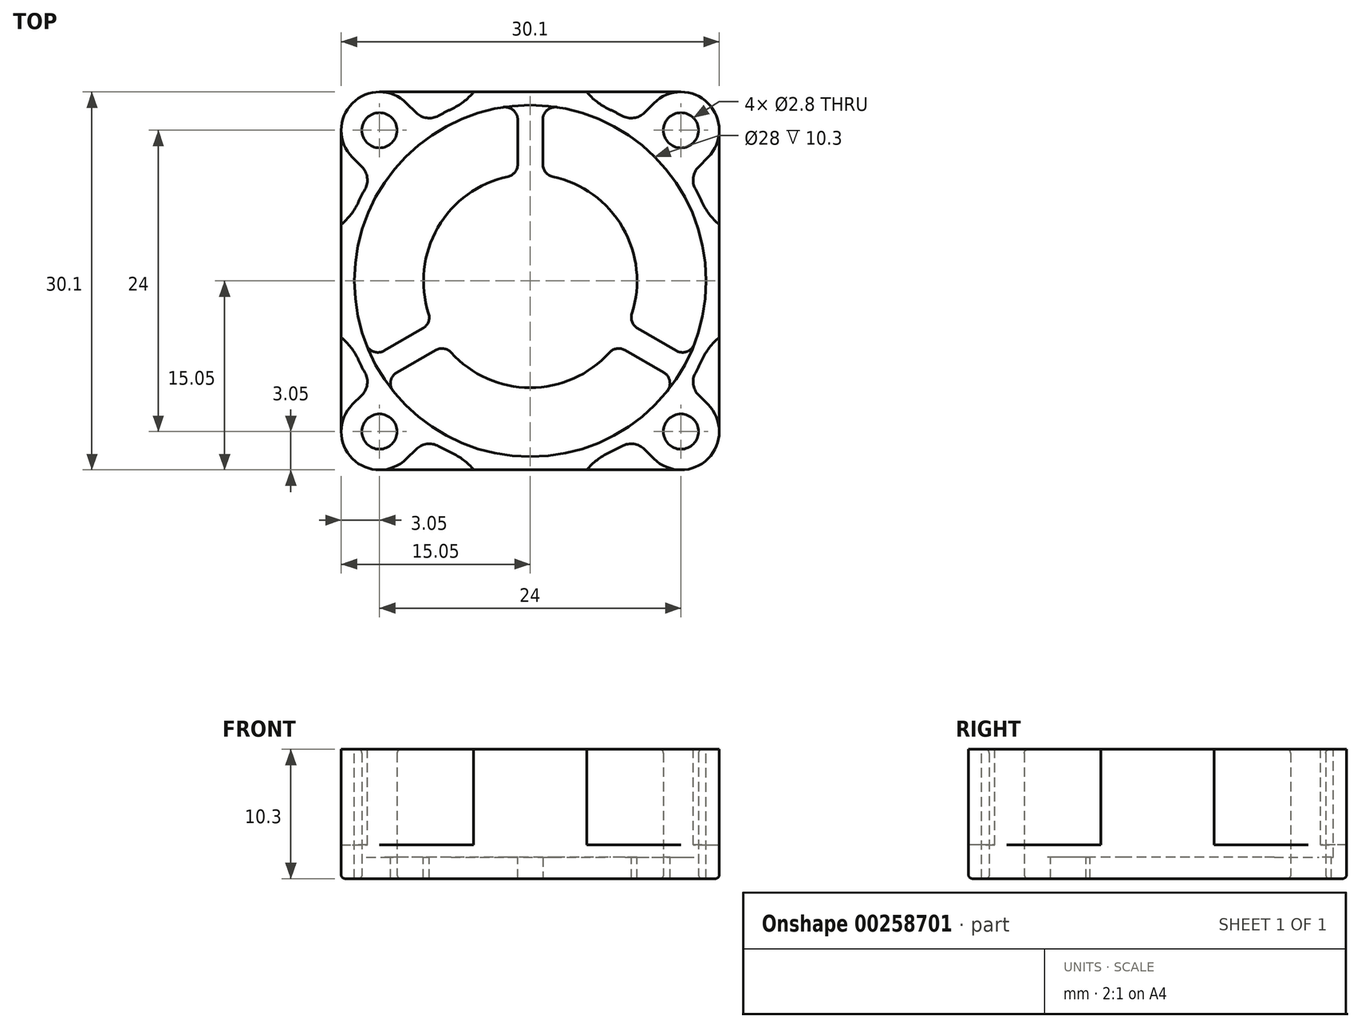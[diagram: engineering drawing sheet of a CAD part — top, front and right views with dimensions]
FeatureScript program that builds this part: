
annotation { "Feature Type Name" : "Feature", "Feature Type Description" : "" }
export const myFeature = defineFeature(function(context is Context, id is Id, definition is map)
    precondition{}
    {
        {
            var Q0;
            Q0=qCreatedBy(makeId("Top.planeOp"),FACE);
            var sketch = newSketch(context, id + "F0", { "sketchPlane" : qUnion([Q0])});
            skLineSegment(sketch, "E0.bottom", {"start": v(-15.05, 15.05) * mm, "end": v(15.05, 15.05) * mm});
            skLineSegment(sketch, "E0.top", {"start": v(-15.05, -15.05) * mm, "end": v(15.05, -15.05) * mm});
            skLineSegment(sketch, "E0.left", {"start": v(-15.05, 15.05) * mm, "end": v(-15.05, -15.05) * mm});
            skLineSegment(sketch, "E0.right", {"start": v(15.05, 15.05) * mm, "end": v(15.05, -15.05) * mm});
            skPoint(sketch, "E0.middle", {"position": v(0, 0) * mm});
            skCircle(sketch, "E1", {"center": v(-12, -12) * mm, "radius": 1.4 * mm});
            skCircle(sketch, "E2", {"center": v(12, -12) * mm, "radius": 1.4 * mm});
            skCircle(sketch, "E3", {"center": v(-12, 12) * mm, "radius": 1.4 * mm});
            skCircle(sketch, "E4", {"center": v(12, 12) * mm, "radius": 1.4 * mm});
            skSolve(sketch);
        }
        {
            var Q0;
            Q0=makeQuery(id+"F0.imprint","IMPRINT",FACE,{"disambiguationData":[TD([[makeQuery(id+"F0.imprint","IMPRINT",EDGE,{"derivedFrom":sQuery(id+"F0.wireOp",EDGE,"E0.bottom")}),-1.0]])]});
            extrude(context, id + "F1", {"entities" : qUnion([Q0]), "depth" : 10.3 * mm});
        }
        {
            var Q0;
            Q0=makeQuery(id+"F1.opExtrude","SWEPT_EDGE",EDGE,{"disambiguationData":[OSD([sQuery(id+"F0.wireOp",EDGE,"E0.top"),sQuery(id+"F0.wireOp",EDGE,"E0.left")])]});
            var Q1;
            Q1=makeQuery(id+"F1.opExtrude","SWEPT_EDGE",EDGE,{"disambiguationData":[OSD([sQuery(id+"F0.wireOp",EDGE,"E0.bottom"),sQuery(id+"F0.wireOp",EDGE,"E0.left")])]});
            var Q2;
            Q2=makeQuery(id+"F1.opExtrude","SWEPT_EDGE",EDGE,{"disambiguationData":[OSD([sQuery(id+"F0.wireOp",EDGE,"E0.top"),sQuery(id+"F0.wireOp",EDGE,"E0.right")])]});
            var Q3;
            Q3=makeQuery(id+"F1.opExtrude","SWEPT_EDGE",EDGE,{"disambiguationData":[OSD([sQuery(id+"F0.wireOp",EDGE,"E0.bottom"),sQuery(id+"F0.wireOp",EDGE,"E0.right")])]});
            fillet(context, id + "F2", {"entities" : qUnion([Q0, Q1, Q2, Q3]), "radius" : 3.05 * mm, "tangentPropagation" : true, "allowEdgeOverflow" : false});
        }
        {
            var Q0;
            Q0=makeQuery(id+"F1.opExtrude","CAP_FACE",FACE,{"disambiguationData":[OSD([sQuery(id+"F0.wireOp",EDGE,"E0.bottom"),sQuery(id+"F0.wireOp",EDGE,"E0.top"),sQuery(id+"F0.wireOp",EDGE,"E0.left"),sQuery(id+"F0.wireOp",EDGE,"E0.right"),sQuery(id+"F0.wireOp",EDGE,"E1"),sQuery(id+"F0.wireOp",EDGE,"E2"),sQuery(id+"F0.wireOp",EDGE,"E3"),sQuery(id+"F0.wireOp",EDGE,"E4")])],"isStart":false});
            var sketch = newSketch(context, id + "F3", { "sketchPlane" : qUnion([Q0])});
            skCircle(sketch, "E5", {"center": v(0, 0) * mm, "radius": 14 * mm});
            skCircle(sketch, "E6", {"center": v(0, 0) * mm, "radius": 15.05 * mm});
            skCircle(sketch, "E7", {"center": v(-12, 12) * mm, "radius": 3.05 * mm});
            skCircle(sketch, "E8", {"center": v(12, 12) * mm, "radius": 3.05 * mm});
            skCircle(sketch, "E9", {"center": v(-12, -12) * mm, "radius": 3.05 * mm});
            skCircle(sketch, "E10", {"center": v(12, -12) * mm, "radius": 3.05 * mm});
            skLineSegment(sketch, "E11", {"start": v(-14.16, 9.84) * mm, "end": v(9.84, -14.16) * mm});
            skLineSegment(sketch, "E12", {"start": v(14.16, -9.84) * mm, "end": v(-9.84, 14.16) * mm});
            skLineSegment(sketch, "E13", {"start": v(9.84, 14.16) * mm, "end": v(-14.16, -9.84) * mm});
            skLineSegment(sketch, "E14", {"start": v(-9.84, -14.16) * mm, "end": v(14.16, 9.84) * mm});
            skLineSegment(sketch, "E15.bottom", {"start": v(-15.05, 4.5) * mm, "end": v(15.05, 4.5) * mm});
            skLineSegment(sketch, "E15.top", {"start": v(-15.05, -4.5) * mm, "end": v(15.05, -4.5) * mm});
            skLineSegment(sketch, "E15.left", {"start": v(-15.05, 4.5) * mm, "end": v(-15.05, -4.5) * mm});
            skLineSegment(sketch, "E15.right", {"start": v(15.05, 4.5) * mm, "end": v(15.05, -4.5) * mm});
            skLineSegment(sketch, "E16.bottom", {"start": v(4.5, 15.05) * mm, "end": v(-4.5, 15.05) * mm});
            skLineSegment(sketch, "E16.top", {"start": v(4.5, -15.05) * mm, "end": v(-4.5, -15.05) * mm});
            skLineSegment(sketch, "E16.left", {"start": v(4.5, 15.05) * mm, "end": v(4.5, -15.05) * mm});
            skLineSegment(sketch, "E16.right", {"start": v(-4.5, 15.05) * mm, "end": v(-4.5, -15.05) * mm});
            skSolve(sketch);
        }
        {
            var Q0;
            {var subQ0=sQuery(id+"F3.wireOp",EDGE,"E11");var subQ3=sQuery(id+"F3.wireOp",EDGE,"E6");var subQ4=makeQuery(id+"F3.imprint","INTERSECT",VERTEX,{"disambiguationData":[OD(0.0)],"derivedFrom":[subQ3,subQ0]});Q0=makeQuery(id+"F3.imprint","IMPRINT",FACE,{"disambiguationData":[TD([[makeQuery(id+"F3.imprint","IMPRINT",EDGE,{"disambiguationData":[TD([[subQ4,-1.0]])],"derivedFrom":subQ3}),-1.0]])]});}
            var Q1;
            {var subQ3=sQuery(id+"F3.wireOp",EDGE,"E6");var subQ7=sQuery(id+"F3.wireOp",EDGE,"E15.top");var subQ9=makeQuery(id+"F3.imprint","INTERSECT",VERTEX,{"disambiguationData":[OD(0.0)],"derivedFrom":[subQ3,subQ7]});Q1=makeQuery(id+"F3.imprint","IMPRINT",FACE,{"disambiguationData":[TD([[makeQuery(id+"F3.imprint","IMPRINT",EDGE,{"disambiguationData":[TD([[subQ9,-1.0]])],"derivedFrom":subQ3}),-1.0]])]});}
            var Q2;
            {var subQ3=sQuery(id+"F3.wireOp",EDGE,"E6");var subQ5=sQuery(id+"F3.wireOp",EDGE,"E14");var subQ8=makeQuery(id+"F3.imprint","INTERSECT",VERTEX,{"disambiguationData":[OD(1.0)],"derivedFrom":[subQ3,subQ5]});Q2=makeQuery(id+"F3.imprint","IMPRINT",FACE,{"disambiguationData":[TD([[makeQuery(id+"F3.imprint","IMPRINT",EDGE,{"disambiguationData":[TD([[subQ8,-1.0]])],"derivedFrom":subQ3}),-1.0]])]});}
            var Q3;
            {var subQ0=sQuery(id+"F3.wireOp",EDGE,"E16.left");var subQ3=sQuery(id+"F3.wireOp",EDGE,"E6");var subQ4=makeQuery(id+"F3.imprint","INTERSECT",VERTEX,{"disambiguationData":[OD(1.0)],"derivedFrom":[subQ3,subQ0]});Q3=makeQuery(id+"F3.imprint","IMPRINT",FACE,{"disambiguationData":[TD([[makeQuery(id+"F3.imprint","IMPRINT",EDGE,{"disambiguationData":[TD([[subQ4,-1.0]])],"derivedFrom":subQ3}),-1.0]])]});}
            var Q4;
            {var subQ0=sQuery(id+"F3.wireOp",EDGE,"E12");var subQ3=sQuery(id+"F3.wireOp",EDGE,"E6");var subQ4=makeQuery(id+"F3.imprint","INTERSECT",VERTEX,{"disambiguationData":[OD(1.0)],"derivedFrom":[subQ3,subQ0]});Q4=makeQuery(id+"F3.imprint","IMPRINT",FACE,{"disambiguationData":[TD([[makeQuery(id+"F3.imprint","IMPRINT",EDGE,{"disambiguationData":[TD([[subQ4,-1.0]])],"derivedFrom":subQ3}),-1.0]])]});}
            var Q5;
            {var subQ0=sQuery(id+"F3.wireOp",EDGE,"E15.bottom");var subQ3=sQuery(id+"F3.wireOp",EDGE,"E6");var subQ4=makeQuery(id+"F3.imprint","INTERSECT",VERTEX,{"disambiguationData":[OD(0.0)],"derivedFrom":[subQ3,subQ0]});Q5=makeQuery(id+"F3.imprint","IMPRINT",FACE,{"disambiguationData":[TD([[makeQuery(id+"F3.imprint","IMPRINT",EDGE,{"disambiguationData":[TD([[subQ4,-1.0]])],"derivedFrom":subQ3}),-1.0]])]});}
            var Q6;
            {var subQ3=sQuery(id+"F3.wireOp",EDGE,"E13");var subQ7=sQuery(id+"F3.wireOp",EDGE,"E6");var subQ9=makeQuery(id+"F3.imprint","INTERSECT",VERTEX,{"disambiguationData":[OD(0.0)],"derivedFrom":[subQ7,subQ3]});Q6=makeQuery(id+"F3.imprint","IMPRINT",FACE,{"disambiguationData":[TD([[makeQuery(id+"F3.imprint","IMPRINT",EDGE,{"disambiguationData":[TD([[subQ9,-1.0]])],"derivedFrom":subQ7}),-1.0]])]});}
            var Q7;
            {var subQ0=sQuery(id+"F3.wireOp",EDGE,"E16.right");var subQ3=sQuery(id+"F3.wireOp",EDGE,"E6");var subQ4=makeQuery(id+"F3.imprint","INTERSECT",VERTEX,{"disambiguationData":[OD(0.0)],"derivedFrom":[subQ3,subQ0]});Q7=makeQuery(id+"F3.imprint","IMPRINT",FACE,{"disambiguationData":[TD([[makeQuery(id+"F3.imprint","IMPRINT",EDGE,{"disambiguationData":[TD([[subQ4,-1.0]])],"derivedFrom":subQ3}),-1.0]])]});}
            var Q8;
            {var subQ1=sQuery(id+"F3.wireOp",EDGE,"E5");var subQ8=sQuery(id+"F3.wireOp",EDGE,"E12");var subQ9=makeQuery(id+"F3.imprint","INTERSECT",VERTEX,{"disambiguationData":[OD(0.0)],"derivedFrom":[subQ1,subQ8]});Q8=makeQuery(id+"F3.imprint","IMPRINT",FACE,{"disambiguationData":[TD([[makeQuery(id+"F3.imprint","IMPRINT",EDGE,{"disambiguationData":[TD([[subQ9,-1.0]])],"derivedFrom":subQ1}),1.0]])]});}
            var Q9;
            {var subQ0=sQuery(id+"F3.wireOp",EDGE,"E11");var subQ1=sQuery(id+"F3.wireOp",EDGE,"E5");var subQ2=makeQuery(id+"F3.imprint","INTERSECT",VERTEX,{"disambiguationData":[OD(0.0)],"derivedFrom":[subQ1,subQ0]});Q9=makeQuery(id+"F3.imprint","IMPRINT",FACE,{"disambiguationData":[TD([[makeQuery(id+"F3.imprint","IMPRINT",EDGE,{"disambiguationData":[TD([[subQ2,-1.0]])],"derivedFrom":subQ1}),1.0]])]});}
            var Q10;
            {var subQ0=sQuery(id+"F3.wireOp",EDGE,"E15.bottom");var subQ1=sQuery(id+"F3.wireOp",EDGE,"E5");var subQ2=makeQuery(id+"F3.imprint","INTERSECT",VERTEX,{"disambiguationData":[OD(1.0)],"derivedFrom":[subQ1,subQ0]});Q10=makeQuery(id+"F3.imprint","IMPRINT",FACE,{"disambiguationData":[TD([[makeQuery(id+"F3.imprint","IMPRINT",EDGE,{"disambiguationData":[TD([[subQ2,-1.0]])],"derivedFrom":subQ1}),1.0]])]});}
            var Q11;
            {var subQ0=sQuery(id+"F3.wireOp",EDGE,"E15.top");var subQ1=sQuery(id+"F3.wireOp",EDGE,"E5");var subQ2=makeQuery(id+"F3.imprint","INTERSECT",VERTEX,{"disambiguationData":[OD(0.0)],"derivedFrom":[subQ1,subQ0]});Q11=makeQuery(id+"F3.imprint","IMPRINT",FACE,{"disambiguationData":[TD([[makeQuery(id+"F3.imprint","IMPRINT",EDGE,{"disambiguationData":[TD([[subQ2,-1.0]])],"derivedFrom":subQ1}),1.0]])]});}
            var Q12;
            {var subQ0=sQuery(id+"F3.wireOp",EDGE,"E13");var subQ1=sQuery(id+"F3.wireOp",EDGE,"E5");var subQ2=makeQuery(id+"F3.imprint","INTERSECT",VERTEX,{"disambiguationData":[OD(1.0)],"derivedFrom":[subQ1,subQ0]});Q12=makeQuery(id+"F3.imprint","IMPRINT",FACE,{"disambiguationData":[TD([[makeQuery(id+"F3.imprint","IMPRINT",EDGE,{"disambiguationData":[TD([[subQ2,-1.0]])],"derivedFrom":subQ1}),1.0]])]});}
            var Q13;
            {var subQ0=sQuery(id+"F3.wireOp",EDGE,"E16.right");var subQ9=sQuery(id+"F3.wireOp",EDGE,"E5");var subQ10=makeQuery(id+"F3.imprint","INTERSECT",VERTEX,{"disambiguationData":[OD(1.0)],"derivedFrom":[subQ9,subQ0]});Q13=makeQuery(id+"F3.imprint","IMPRINT",FACE,{"disambiguationData":[TD([[makeQuery(id+"F3.imprint","IMPRINT",EDGE,{"disambiguationData":[TD([[subQ10,-1.0]])],"derivedFrom":subQ9}),1.0]])]});}
            var Q14;
            {var subQ0=sQuery(id+"F3.wireOp",EDGE,"E14");var subQ1=sQuery(id+"F3.wireOp",EDGE,"E5");var subQ2=makeQuery(id+"F3.imprint","INTERSECT",VERTEX,{"disambiguationData":[OD(1.0)],"derivedFrom":[subQ1,subQ0]});Q14=makeQuery(id+"F3.imprint","IMPRINT",FACE,{"disambiguationData":[TD([[makeQuery(id+"F3.imprint","IMPRINT",EDGE,{"disambiguationData":[TD([[subQ2,-1.0]])],"derivedFrom":subQ1}),1.0]])]});}
            var Q15;
            {var subQ0=sQuery(id+"F3.wireOp",EDGE,"E16.left");var subQ1=sQuery(id+"F3.wireOp",EDGE,"E5");var subQ2=makeQuery(id+"F3.imprint","INTERSECT",VERTEX,{"disambiguationData":[OD(1.0)],"derivedFrom":[subQ1,subQ0]});Q15=makeQuery(id+"F3.imprint","IMPRINT",FACE,{"disambiguationData":[TD([[makeQuery(id+"F3.imprint","IMPRINT",EDGE,{"disambiguationData":[TD([[subQ2,-1.0]])],"derivedFrom":subQ1}),1.0]])]});}
            var Q16;
            {var subQ0=sQuery(id+"F3.wireOp",EDGE,"E11");var subQ1=sQuery(id+"F3.wireOp",EDGE,"E5");var subQ2=makeQuery(id+"F3.imprint","INTERSECT",VERTEX,{"disambiguationData":[OD(1.0)],"derivedFrom":[subQ1,subQ0]});Q16=makeQuery(id+"F3.imprint","IMPRINT",FACE,{"disambiguationData":[TD([[makeQuery(id+"F3.imprint","IMPRINT",EDGE,{"disambiguationData":[TD([[subQ2,-1.0]])],"derivedFrom":subQ1}),1.0]])]});}
            var Q17;
            {var subQ0=sQuery(id+"F3.wireOp",EDGE,"E12");var subQ1=sQuery(id+"F3.wireOp",EDGE,"E5");var subQ2=makeQuery(id+"F3.imprint","INTERSECT",VERTEX,{"disambiguationData":[OD(1.0)],"derivedFrom":[subQ1,subQ0]});Q17=makeQuery(id+"F3.imprint","IMPRINT",FACE,{"disambiguationData":[TD([[makeQuery(id+"F3.imprint","IMPRINT",EDGE,{"disambiguationData":[TD([[subQ2,-1.0]])],"derivedFrom":subQ1}),1.0]])]});}
            var Q18;
            {var subQ0=sQuery(id+"F3.wireOp",EDGE,"E15.bottom");var subQ1=sQuery(id+"F3.wireOp",EDGE,"E5");var subQ2=makeQuery(id+"F3.imprint","INTERSECT",VERTEX,{"disambiguationData":[OD(0.0)],"derivedFrom":[subQ1,subQ0]});Q18=makeQuery(id+"F3.imprint","IMPRINT",FACE,{"disambiguationData":[TD([[makeQuery(id+"F3.imprint","IMPRINT",EDGE,{"disambiguationData":[TD([[subQ2,1.0]])],"derivedFrom":subQ1}),1.0]])]});}
            var Q19;
            {var subQ0=sQuery(id+"F3.wireOp",EDGE,"E14");var subQ1=sQuery(id+"F3.wireOp",EDGE,"E5");var subQ2=makeQuery(id+"F3.imprint","INTERSECT",VERTEX,{"disambiguationData":[OD(0.0)],"derivedFrom":[subQ1,subQ0]});Q19=makeQuery(id+"F3.imprint","IMPRINT",FACE,{"disambiguationData":[TD([[makeQuery(id+"F3.imprint","IMPRINT",EDGE,{"disambiguationData":[TD([[subQ2,1.0]])],"derivedFrom":subQ1}),1.0]])]});}
            var Q20;
            {var subQ1=sQuery(id+"F3.wireOp",EDGE,"E5");var subQ9=sQuery(id+"F3.wireOp",EDGE,"E14");var subQ12=makeQuery(id+"F3.imprint","INTERSECT",VERTEX,{"disambiguationData":[OD(0.0)],"derivedFrom":[subQ1,subQ9]});Q20=makeQuery(id+"F3.imprint","IMPRINT",FACE,{"disambiguationData":[TD([[makeQuery(id+"F3.imprint","IMPRINT",EDGE,{"disambiguationData":[TD([[subQ12,-1.0]])],"derivedFrom":subQ1}),1.0]])]});}
            var Q21;
            {var subQ0=sQuery(id+"F3.wireOp",EDGE,"E13");var subQ1=sQuery(id+"F3.wireOp",EDGE,"E5");var subQ2=makeQuery(id+"F3.imprint","INTERSECT",VERTEX,{"disambiguationData":[OD(0.0)],"derivedFrom":[subQ1,subQ0]});Q21=makeQuery(id+"F3.imprint","IMPRINT",FACE,{"disambiguationData":[TD([[makeQuery(id+"F3.imprint","IMPRINT",EDGE,{"disambiguationData":[TD([[subQ2,-1.0]])],"derivedFrom":subQ1}),1.0]])]});}
            var Q22;
            {var subQ5=sQuery(id+"F3.wireOp",EDGE,"E16.left");var subQ9=sQuery(id+"F3.wireOp",EDGE,"E5");var subQ10=makeQuery(id+"F3.imprint","INTERSECT",VERTEX,{"disambiguationData":[OD(0.0)],"derivedFrom":[subQ9,subQ5]});Q22=makeQuery(id+"F3.imprint","IMPRINT",FACE,{"disambiguationData":[TD([[makeQuery(id+"F3.imprint","IMPRINT",EDGE,{"disambiguationData":[TD([[subQ10,-1.0]])],"derivedFrom":subQ9}),1.0]])]});}
            var Q23;
            {var subQ0=sQuery(id+"F3.wireOp",EDGE,"E16.right");var subQ1=sQuery(id+"F3.wireOp",EDGE,"E5");var subQ2=makeQuery(id+"F3.imprint","INTERSECT",VERTEX,{"disambiguationData":[OD(0.0)],"derivedFrom":[subQ1,subQ0]});Q23=makeQuery(id+"F3.imprint","IMPRINT",FACE,{"disambiguationData":[TD([[makeQuery(id+"F3.imprint","IMPRINT",EDGE,{"disambiguationData":[TD([[subQ2,-1.0]])],"derivedFrom":subQ1}),1.0]])]});}
            var Q24;
            {var subQ0=sQuery(id+"F3.wireOp",EDGE,"E15.bottom");var subQ1=sQuery(id+"F3.wireOp",EDGE,"E12");var subQ2=makeQuery(id+"F3.imprint","INTERSECT",VERTEX,{"derivedFrom":[subQ1,subQ0]});Q24=makeQuery(id+"F3.imprint","IMPRINT",FACE,{"disambiguationData":[TD([[makeQuery(id+"F3.imprint","IMPRINT",EDGE,{"disambiguationData":[TD([[subQ2,-1.0]])],"derivedFrom":subQ1}),1.0]])]});}
            var Q25;
            {var subQ0=sQuery(id+"F3.wireOp",EDGE,"E15.bottom");var subQ1=sQuery(id+"F3.wireOp",EDGE,"E11");var subQ2=makeQuery(id+"F3.imprint","INTERSECT",VERTEX,{"derivedFrom":[subQ1,subQ0]});Q25=makeQuery(id+"F3.imprint","IMPRINT",FACE,{"disambiguationData":[TD([[makeQuery(id+"F3.imprint","IMPRINT",EDGE,{"disambiguationData":[TD([[subQ2,-1.0]])],"derivedFrom":subQ1}),1.0]])]});}
            var Q26;
            {var subQ3=sQuery(id+"F3.wireOp",EDGE,"E16.right");var subQ6=sQuery(id+"F3.wireOp",EDGE,"E11");var subQ9=makeQuery(id+"F3.imprint","INTERSECT",VERTEX,{"derivedFrom":[subQ6,subQ3]});Q26=makeQuery(id+"F3.imprint","IMPRINT",FACE,{"disambiguationData":[TD([[makeQuery(id+"F3.imprint","IMPRINT",EDGE,{"disambiguationData":[TD([[subQ9,-1.0]])],"derivedFrom":subQ6}),1.0]])]});}
            var Q27;
            {var subQ0=sQuery(id+"F3.wireOp",EDGE,"E13");var subQ1=sQuery(id+"F3.wireOp",EDGE,"E11");var subQ2=makeQuery(id+"F3.imprint","INTERSECT",VERTEX,{"derivedFrom":[subQ1,subQ0]});Q27=makeQuery(id+"F3.imprint","IMPRINT",FACE,{"disambiguationData":[TD([[makeQuery(id+"F3.imprint","IMPRINT",EDGE,{"disambiguationData":[TD([[subQ2,-1.0]])],"derivedFrom":subQ1}),1.0]])]});}
            var Q28;
            {var subQ1=sQuery(id+"F3.wireOp",EDGE,"E11");var subQ5=sQuery(id+"F3.wireOp",EDGE,"E13");var subQ6=makeQuery(id+"F3.imprint","INTERSECT",VERTEX,{"derivedFrom":[subQ1,subQ5]});Q28=makeQuery(id+"F3.imprint","IMPRINT",FACE,{"disambiguationData":[TD([[makeQuery(id+"F3.imprint","IMPRINT",EDGE,{"disambiguationData":[TD([[subQ6,-1.0]])],"derivedFrom":subQ1}),-1.0]])]});}
            var Q29;
            {var subQ0=sQuery(id+"F3.wireOp",EDGE,"E16.right");var subQ1=sQuery(id+"F3.wireOp",EDGE,"E13");var subQ2=makeQuery(id+"F3.imprint","INTERSECT",VERTEX,{"derivedFrom":[subQ1,subQ0]});Q29=makeQuery(id+"F3.imprint","IMPRINT",FACE,{"disambiguationData":[TD([[makeQuery(id+"F3.imprint","IMPRINT",EDGE,{"disambiguationData":[TD([[subQ2,-1.0]])],"derivedFrom":subQ1}),1.0]])]});}
            var Q30;
            {var subQ0=sQuery(id+"F3.wireOp",EDGE,"E16.right");var subQ1=sQuery(id+"F3.wireOp",EDGE,"E14");var subQ2=makeQuery(id+"F3.imprint","INTERSECT",VERTEX,{"derivedFrom":[subQ1,subQ0]});Q30=makeQuery(id+"F3.imprint","IMPRINT",FACE,{"disambiguationData":[TD([[makeQuery(id+"F3.imprint","IMPRINT",EDGE,{"disambiguationData":[TD([[subQ2,-1.0]])],"derivedFrom":subQ1}),1.0]])]});}
            var Q31;
            {var subQ0=sQuery(id+"F3.wireOp",EDGE,"E15.top");var subQ1=sQuery(id+"F3.wireOp",EDGE,"E11");var subQ2=makeQuery(id+"F3.imprint","INTERSECT",VERTEX,{"derivedFrom":[subQ1,subQ0]});Q31=makeQuery(id+"F3.imprint","IMPRINT",FACE,{"disambiguationData":[TD([[makeQuery(id+"F3.imprint","IMPRINT",EDGE,{"disambiguationData":[TD([[subQ2,-1.0]])],"derivedFrom":subQ1}),1.0]])]});}
            var Q32;
            {var subQ0=sQuery(id+"F3.wireOp",EDGE,"E15.top");var subQ1=sQuery(id+"F3.wireOp",EDGE,"E12");var subQ2=makeQuery(id+"F3.imprint","INTERSECT",VERTEX,{"derivedFrom":[subQ1,subQ0]});Q32=makeQuery(id+"F3.imprint","IMPRINT",FACE,{"disambiguationData":[TD([[makeQuery(id+"F3.imprint","IMPRINT",EDGE,{"disambiguationData":[TD([[subQ2,-1.0]])],"derivedFrom":subQ1}),1.0]])]});}
            var Q33;
            {var subQ0=sQuery(id+"F3.wireOp",EDGE,"E16.left");var subQ1=sQuery(id+"F3.wireOp",EDGE,"E14");var subQ2=makeQuery(id+"F3.imprint","INTERSECT",VERTEX,{"derivedFrom":[subQ1,subQ0]});Q33=makeQuery(id+"F3.imprint","IMPRINT",FACE,{"disambiguationData":[TD([[makeQuery(id+"F3.imprint","IMPRINT",EDGE,{"disambiguationData":[TD([[subQ2,-1.0]])],"derivedFrom":subQ1}),1.0]])]});}
            var Q34;
            {var subQ1=sQuery(id+"F3.wireOp",EDGE,"E11");var subQ5=sQuery(id+"F3.wireOp",EDGE,"E14");var subQ6=makeQuery(id+"F3.imprint","INTERSECT",VERTEX,{"derivedFrom":[subQ1,subQ5]});Q34=makeQuery(id+"F3.imprint","IMPRINT",FACE,{"disambiguationData":[TD([[makeQuery(id+"F3.imprint","IMPRINT",EDGE,{"disambiguationData":[TD([[subQ6,-1.0]])],"derivedFrom":subQ1}),1.0]])]});}
            var Q35;
            {var subQ0=sQuery(id+"F3.wireOp",EDGE,"E16.left");var subQ1=sQuery(id+"F3.wireOp",EDGE,"E12");var subQ2=makeQuery(id+"F3.imprint","INTERSECT",VERTEX,{"derivedFrom":[subQ1,subQ0]});Q35=makeQuery(id+"F3.imprint","IMPRINT",FACE,{"disambiguationData":[TD([[makeQuery(id+"F3.imprint","IMPRINT",EDGE,{"disambiguationData":[TD([[subQ2,-1.0]])],"derivedFrom":subQ1}),-1.0]])]});}
            var Q36;
            {var subQ0=sQuery(id+"F3.wireOp",EDGE,"E14");var subQ1=sQuery(id+"F3.wireOp",EDGE,"E11");var subQ2=makeQuery(id+"F3.imprint","INTERSECT",VERTEX,{"derivedFrom":[subQ1,subQ0]});Q36=makeQuery(id+"F3.imprint","IMPRINT",FACE,{"disambiguationData":[TD([[makeQuery(id+"F3.imprint","IMPRINT",EDGE,{"disambiguationData":[TD([[subQ2,-1.0]])],"derivedFrom":subQ1}),-1.0]])]});}
            var Q37;
            {var subQ0=sQuery(id+"F3.wireOp",EDGE,"E16.right");var subQ1=sQuery(id+"F3.wireOp",EDGE,"E11");var subQ2=makeQuery(id+"F3.imprint","INTERSECT",VERTEX,{"derivedFrom":[subQ1,subQ0]});Q37=makeQuery(id+"F3.imprint","IMPRINT",FACE,{"disambiguationData":[TD([[makeQuery(id+"F3.imprint","IMPRINT",EDGE,{"disambiguationData":[TD([[subQ2,-1.0]])],"derivedFrom":subQ1}),-1.0]])]});}
            var Q38;
            {var subQ0=sQuery(id+"F3.wireOp",EDGE,"E13");var subQ1=sQuery(id+"F3.wireOp",EDGE,"E12");var subQ2=makeQuery(id+"F3.imprint","INTERSECT",VERTEX,{"derivedFrom":[subQ1,subQ0]});Q38=makeQuery(id+"F3.imprint","IMPRINT",FACE,{"disambiguationData":[TD([[makeQuery(id+"F3.imprint","IMPRINT",EDGE,{"disambiguationData":[TD([[subQ2,-1.0]])],"derivedFrom":subQ1}),-1.0]])]});}
            var Q39;
            {var subQ0=sQuery(id+"F3.wireOp",EDGE,"E14");var subQ1=sQuery(id+"F3.wireOp",EDGE,"E12");var subQ2=makeQuery(id+"F3.imprint","INTERSECT",VERTEX,{"derivedFrom":[subQ1,subQ0]});Q39=makeQuery(id+"F3.imprint","IMPRINT",FACE,{"disambiguationData":[TD([[makeQuery(id+"F3.imprint","IMPRINT",EDGE,{"disambiguationData":[TD([[subQ2,-1.0]])],"derivedFrom":subQ1}),-1.0]])]});}
            var Q40;
            {var subQ0=sQuery(id+"F3.wireOp",EDGE,"E16.left");var subQ1=sQuery(id+"F3.wireOp",EDGE,"E13");var subQ2=makeQuery(id+"F3.imprint","INTERSECT",VERTEX,{"derivedFrom":[subQ1,subQ0]});Q40=makeQuery(id+"F3.imprint","IMPRINT",FACE,{"disambiguationData":[TD([[makeQuery(id+"F3.imprint","IMPRINT",EDGE,{"disambiguationData":[TD([[subQ2,-1.0]])],"derivedFrom":subQ1}),1.0]])]});}
            var Q41;
            {var subQ0=sQuery(id+"F3.wireOp",EDGE,"E7");var subQ1=sQuery(id+"F3.wireOp",EDGE,"E5");var subQ2=makeQuery(id+"F3.imprint","INTERSECT",VERTEX,{"disambiguationData":[OD(0.0)],"derivedFrom":[subQ1,subQ0]});Q41=makeQuery(id+"F3.imprint","IMPRINT",FACE,{"disambiguationData":[TD([[makeQuery(id+"F3.imprint","IMPRINT",EDGE,{"disambiguationData":[TD([[subQ2,-1.0]])],"derivedFrom":subQ1}),1.0]])]});}
            var Q42;
            {var subQ0=sQuery(id+"F3.wireOp",EDGE,"E8");var subQ1=sQuery(id+"F3.wireOp",EDGE,"E5");var subQ2=makeQuery(id+"F3.imprint","INTERSECT",VERTEX,{"disambiguationData":[OD(0.0)],"derivedFrom":[subQ1,subQ0]});Q42=makeQuery(id+"F3.imprint","IMPRINT",FACE,{"disambiguationData":[TD([[makeQuery(id+"F3.imprint","IMPRINT",EDGE,{"disambiguationData":[TD([[subQ2,-1.0]])],"derivedFrom":subQ1}),1.0]])]});}
            var Q43;
            {var subQ0=sQuery(id+"F3.wireOp",EDGE,"E9");var subQ1=sQuery(id+"F3.wireOp",EDGE,"E5");var subQ2=makeQuery(id+"F3.imprint","INTERSECT",VERTEX,{"disambiguationData":[OD(0.0)],"derivedFrom":[subQ1,subQ0]});Q43=makeQuery(id+"F3.imprint","IMPRINT",FACE,{"disambiguationData":[TD([[makeQuery(id+"F3.imprint","IMPRINT",EDGE,{"disambiguationData":[TD([[subQ2,-1.0]])],"derivedFrom":subQ1}),1.0]])]});}
            var Q44;
            {var subQ0=sQuery(id+"F3.wireOp",EDGE,"E10");var subQ1=sQuery(id+"F3.wireOp",EDGE,"E5");var subQ2=makeQuery(id+"F3.imprint","INTERSECT",VERTEX,{"disambiguationData":[OD(0.0)],"derivedFrom":[subQ1,subQ0]});Q44=makeQuery(id+"F3.imprint","IMPRINT",FACE,{"disambiguationData":[TD([[makeQuery(id+"F3.imprint","IMPRINT",EDGE,{"disambiguationData":[TD([[subQ2,-1.0]])],"derivedFrom":subQ1}),1.0]])]});}
            extrude(context, id + "F4", {"entities" : qUnion([Q0, Q1, Q2, Q3, Q4, Q5, Q6, Q7, Q8, Q9, Q10, Q11, Q12, Q13, Q14, Q15, Q16, Q17, Q18, Q19, Q20, Q21, Q22, Q23, Q24, Q25, Q26, Q27, Q28, Q29, Q30, Q31, Q32, Q33, Q34, Q35, Q36, Q37, Q38, Q39, Q40, Q41, Q42, Q43, Q44]), "operationType" : NewBodyOperationType.REMOVE, "oppositeDirection" : true, "depth" : 7.6 * mm});
        }
        {
            var Q0;
            Q0=makeQuery(id+"F4.boolean.opBoolean","COPY",FACE,{"derivedFrom":makeQuery(id+"F4.opExtrude","CAP_FACE",FACE,{"disambiguationData":[OSD([sQuery(id+"F3.wireOp",EDGE,"E5")])],"isStart":false})});
            var sketch = newSketch(context, id + "F5", { "sketchPlane" : qUnion([Q0])});
            skCircle(sketch, "E17", {"center": v(0, 0) * mm, "radius": 8.5 * mm});
            skLineSegment(sketch, "E18", {"start": v(-1, 8.44) * mm, "end": v(-1, 13.96) * mm});
            skLineSegment(sketch, "E19", {"start": v(1, 8.44) * mm, "end": v(1, 13.96) * mm});
            skLineSegment(sketch, "E20.1.0", {"start": v(-7.81, -3.35) * mm, "end": v(-12.6, -6.12) * mm});
            skLineSegment(sketch, "E20.1.1", {"start": v(-6.81, -5.09) * mm, "end": v(-11.6, -7.85) * mm});
            skLineSegment(sketch, "E20.2.0", {"start": v(6.81, -5.09) * mm, "end": v(11.6, -7.85) * mm});
            skLineSegment(sketch, "E20.2.1", {"start": v(7.81, -3.35) * mm, "end": v(12.6, -6.12) * mm});
            skSolve(sketch);
        }
        {
            var Q0;
            {var subQ0=sQuery(id+"F5.wireOp",EDGE,"E18");Q0=makeQuery(id+"F5.imprint","IMPRINT",FACE,{"disambiguationData":[TD([[makeQuery(id+"F5.imprint","IMPRINT",EDGE,{"derivedFrom":subQ0}),1.0]])]});}
            var Q1;
            {var subQ0=sQuery(id+"F5.wireOp",EDGE,"E19");Q1=makeQuery(id+"F5.imprint","IMPRINT",FACE,{"disambiguationData":[TD([[makeQuery(id+"F5.imprint","IMPRINT",EDGE,{"derivedFrom":subQ0}),-1.0]])]});}
            var Q2;
            {var subQ0=sQuery(id+"F5.wireOp",EDGE,"E20.1.1");Q2=makeQuery(id+"F5.imprint","IMPRINT",FACE,{"disambiguationData":[TD([[makeQuery(id+"F5.imprint","IMPRINT",EDGE,{"derivedFrom":subQ0}),1.0]])]});}
            var Q3;
            Q3=makeQuery(id+"F1.opExtrude","CAP_FACE",FACE,{"disambiguationData":[OSD([sQuery(id+"F0.wireOp",EDGE,"E0.bottom"),sQuery(id+"F0.wireOp",EDGE,"E0.top"),sQuery(id+"F0.wireOp",EDGE,"E0.left"),sQuery(id+"F0.wireOp",EDGE,"E0.right"),sQuery(id+"F0.wireOp",EDGE,"E1"),sQuery(id+"F0.wireOp",EDGE,"E2"),sQuery(id+"F0.wireOp",EDGE,"E3"),sQuery(id+"F0.wireOp",EDGE,"E4")])],"isStart":true});
            extrude(context, id + "F6", {"entities" : qUnion([Q0, Q1, Q2]), "operationType" : NewBodyOperationType.REMOVE, "endBound" : BoundingType.UP_TO_SURFACE, "oppositeDirection" : true, "endBoundEntityFace" : qUnion([Q3]), "depth" : 25 * mm});
        }
        {
            var Q0;
            {var subQ0=sQuery(id+"F3.wireOp",EDGE,"E16.left");var subQ1=sQuery(id+"F3.wireOp",EDGE,"E6");Q0=makeQuery(id+"F4.boolean.opBoolean","COPY",EDGE,{"derivedFrom":makeQuery(id+"F4.opExtrude","SWEPT_EDGE",EDGE,{"disambiguationData":[OSD([subQ1,subQ0]),TDD([makeQuery(id+"F3.imprint","INTERSECT",VERTEX,{"disambiguationData":[OD(1.0)],"derivedFrom":[subQ1,subQ0]})])]})});}
            var Q1;
            {var subQ0=sQuery(id+"F3.wireOp",EDGE,"E15.top");var subQ1=sQuery(id+"F3.wireOp",EDGE,"E6");Q1=makeQuery(id+"F4.boolean.opBoolean","COPY",EDGE,{"derivedFrom":makeQuery(id+"F4.opExtrude","SWEPT_EDGE",EDGE,{"disambiguationData":[OSD([subQ1,subQ0]),TDD([makeQuery(id+"F3.imprint","INTERSECT",VERTEX,{"disambiguationData":[OD(1.0)],"derivedFrom":[subQ1,subQ0]})])]})});}
            var Q2;
            {var subQ0=sQuery(id+"F3.wireOp",EDGE,"E15.bottom");var subQ1=sQuery(id+"F3.wireOp",EDGE,"E6");Q2=makeQuery(id+"F4.boolean.opBoolean","COPY",EDGE,{"derivedFrom":makeQuery(id+"F4.opExtrude","SWEPT_EDGE",EDGE,{"disambiguationData":[OSD([subQ1,subQ0]),TDD([makeQuery(id+"F3.imprint","INTERSECT",VERTEX,{"disambiguationData":[OD(0.0)],"derivedFrom":[subQ1,subQ0]})])]})});}
            var Q3;
            {var subQ0=sQuery(id+"F3.wireOp",EDGE,"E16.left");var subQ1=sQuery(id+"F3.wireOp",EDGE,"E6");Q3=makeQuery(id+"F4.boolean.opBoolean","COPY",EDGE,{"derivedFrom":makeQuery(id+"F4.opExtrude","SWEPT_EDGE",EDGE,{"disambiguationData":[OSD([subQ1,subQ0]),TDD([makeQuery(id+"F3.imprint","INTERSECT",VERTEX,{"disambiguationData":[OD(0.0)],"derivedFrom":[subQ1,subQ0]})])]})});}
            var Q4;
            {var subQ0=sQuery(id+"F3.wireOp",EDGE,"E16.right");var subQ1=sQuery(id+"F3.wireOp",EDGE,"E6");Q4=makeQuery(id+"F4.boolean.opBoolean","COPY",EDGE,{"derivedFrom":makeQuery(id+"F4.opExtrude","SWEPT_EDGE",EDGE,{"disambiguationData":[OSD([subQ1,subQ0]),TDD([makeQuery(id+"F3.imprint","INTERSECT",VERTEX,{"disambiguationData":[OD(0.0)],"derivedFrom":[subQ1,subQ0]})])]})});}
            var Q5;
            {var subQ0=sQuery(id+"F3.wireOp",EDGE,"E15.bottom");var subQ1=sQuery(id+"F3.wireOp",EDGE,"E6");Q5=makeQuery(id+"F4.boolean.opBoolean","COPY",EDGE,{"derivedFrom":makeQuery(id+"F4.opExtrude","SWEPT_EDGE",EDGE,{"disambiguationData":[OSD([subQ1,subQ0]),TDD([makeQuery(id+"F3.imprint","INTERSECT",VERTEX,{"disambiguationData":[OD(1.0)],"derivedFrom":[subQ1,subQ0]})])]})});}
            var Q6;
            {var subQ0=sQuery(id+"F3.wireOp",EDGE,"E15.top");var subQ1=sQuery(id+"F3.wireOp",EDGE,"E6");Q6=makeQuery(id+"F4.boolean.opBoolean","COPY",EDGE,{"derivedFrom":makeQuery(id+"F4.opExtrude","SWEPT_EDGE",EDGE,{"disambiguationData":[OSD([subQ1,subQ0]),TDD([makeQuery(id+"F3.imprint","INTERSECT",VERTEX,{"disambiguationData":[OD(0.0)],"derivedFrom":[subQ1,subQ0]})])]})});}
            var Q7;
            {var subQ0=sQuery(id+"F3.wireOp",EDGE,"E16.right");var subQ1=sQuery(id+"F3.wireOp",EDGE,"E6");Q7=makeQuery(id+"F4.boolean.opBoolean","COPY",EDGE,{"derivedFrom":makeQuery(id+"F4.opExtrude","SWEPT_EDGE",EDGE,{"disambiguationData":[OSD([subQ1,subQ0]),TDD([makeQuery(id+"F3.imprint","INTERSECT",VERTEX,{"disambiguationData":[OD(1.0)],"derivedFrom":[subQ1,subQ0]})])]})});}
            fillet(context, id + "F7", {"entities" : qUnion([Q0, Q1, Q2, Q3, Q4, Q5, Q6, Q7]), "radius" : 5 * mm, "tangentPropagation" : true, "allowEdgeOverflow" : false});
        }
        {
            var Q0;
            {var subQ0=sQuery(id+"F3.wireOp",EDGE,"E14");var subQ1=sQuery(id+"F3.wireOp",EDGE,"E6");Q0=makeQuery(id+"F4.boolean.opBoolean","COPY",EDGE,{"derivedFrom":makeQuery(id+"F4.opExtrude","SWEPT_EDGE",EDGE,{"disambiguationData":[OSD([subQ1,subQ0]),TDD([makeQuery(id+"F3.imprint","INTERSECT",VERTEX,{"disambiguationData":[OD(1.0)],"derivedFrom":[subQ1,subQ0]})])]})});}
            var Q1;
            {var subQ0=sQuery(id+"F3.wireOp",EDGE,"E11");var subQ1=sQuery(id+"F3.wireOp",EDGE,"E6");Q1=makeQuery(id+"F4.boolean.opBoolean","COPY",EDGE,{"derivedFrom":makeQuery(id+"F4.opExtrude","SWEPT_EDGE",EDGE,{"disambiguationData":[OSD([subQ1,subQ0]),TDD([makeQuery(id+"F3.imprint","INTERSECT",VERTEX,{"disambiguationData":[OD(1.0)],"derivedFrom":[subQ1,subQ0]})])]})});}
            var Q2;
            {var subQ0=sQuery(id+"F3.wireOp",EDGE,"E12");var subQ1=sQuery(id+"F3.wireOp",EDGE,"E6");Q2=makeQuery(id+"F4.boolean.opBoolean","COPY",EDGE,{"derivedFrom":makeQuery(id+"F4.opExtrude","SWEPT_EDGE",EDGE,{"disambiguationData":[OSD([subQ1,subQ0]),TDD([makeQuery(id+"F3.imprint","INTERSECT",VERTEX,{"disambiguationData":[OD(1.0)],"derivedFrom":[subQ1,subQ0]})])]})});}
            var Q3;
            {var subQ0=sQuery(id+"F3.wireOp",EDGE,"E14");var subQ1=sQuery(id+"F3.wireOp",EDGE,"E6");Q3=makeQuery(id+"F4.boolean.opBoolean","COPY",EDGE,{"derivedFrom":makeQuery(id+"F4.opExtrude","SWEPT_EDGE",EDGE,{"disambiguationData":[OSD([subQ1,subQ0]),TDD([makeQuery(id+"F3.imprint","INTERSECT",VERTEX,{"disambiguationData":[OD(0.0)],"derivedFrom":[subQ1,subQ0]})])]})});}
            var Q4;
            {var subQ0=sQuery(id+"F3.wireOp",EDGE,"E13");var subQ1=sQuery(id+"F3.wireOp",EDGE,"E6");Q4=makeQuery(id+"F4.boolean.opBoolean","COPY",EDGE,{"derivedFrom":makeQuery(id+"F4.opExtrude","SWEPT_EDGE",EDGE,{"disambiguationData":[OSD([subQ1,subQ0]),TDD([makeQuery(id+"F3.imprint","INTERSECT",VERTEX,{"disambiguationData":[OD(0.0)],"derivedFrom":[subQ1,subQ0]})])]})});}
            var Q5;
            {var subQ0=sQuery(id+"F3.wireOp",EDGE,"E12");var subQ1=sQuery(id+"F3.wireOp",EDGE,"E6");Q5=makeQuery(id+"F4.boolean.opBoolean","COPY",EDGE,{"derivedFrom":makeQuery(id+"F4.opExtrude","SWEPT_EDGE",EDGE,{"disambiguationData":[OSD([subQ1,subQ0]),TDD([makeQuery(id+"F3.imprint","INTERSECT",VERTEX,{"disambiguationData":[OD(0.0)],"derivedFrom":[subQ1,subQ0]})])]})});}
            var Q6;
            {var subQ0=sQuery(id+"F3.wireOp",EDGE,"E11");var subQ1=sQuery(id+"F3.wireOp",EDGE,"E6");Q6=makeQuery(id+"F4.boolean.opBoolean","COPY",EDGE,{"derivedFrom":makeQuery(id+"F4.opExtrude","SWEPT_EDGE",EDGE,{"disambiguationData":[OSD([subQ1,subQ0]),TDD([makeQuery(id+"F3.imprint","INTERSECT",VERTEX,{"disambiguationData":[OD(0.0)],"derivedFrom":[subQ1,subQ0]})])]})});}
            var Q7;
            {var subQ0=sQuery(id+"F3.wireOp",EDGE,"E13");var subQ1=sQuery(id+"F3.wireOp",EDGE,"E6");Q7=makeQuery(id+"F4.boolean.opBoolean","COPY",EDGE,{"derivedFrom":makeQuery(id+"F4.opExtrude","SWEPT_EDGE",EDGE,{"disambiguationData":[OSD([subQ1,subQ0]),TDD([makeQuery(id+"F3.imprint","INTERSECT",VERTEX,{"disambiguationData":[OD(1.0)],"derivedFrom":[subQ1,subQ0]})])]})});}
            fillet(context, id + "F8", {"entities" : qUnion([Q0, Q1, Q2, Q3, Q4, Q5, Q6, Q7]), "radius" : 1.5 * mm, "tangentPropagation" : true, "allowEdgeOverflow" : false});
        }
        {
            var Q0;
            Q0=makeQuery(id+"F4.boolean.opBoolean","COPY",FACE,{"derivedFrom":makeQuery(id+"F4.opExtrude","CAP_FACE",FACE,{"disambiguationData":[OSD([sQuery(id+"F3.wireOp",EDGE,"E5")])],"isStart":false})});
            extrude(context, id + "F9", {"entities" : qUnion([Q0]), "operationType" : NewBodyOperationType.REMOVE, "oppositeDirection" : true, "depth" : 1 * mm});
        }
        {
            var Q0;
            {var subQ0=sQuery(id+"F0.wireOp",EDGE,"E0.right");var subQ1=sQuery(id+"F0.wireOp",EDGE,"E0.bottom");Q0=makeQuery(id+"F2.opFillet","BLEND_EDGE",EDGE,{"blendedFrom":[makeQuery(id+"F1.opExtrude","SWEPT_EDGE",EDGE,{"disambiguationData":[OSD([subQ1,subQ0])]}),makeQuery(id+"F1.opExtrude","CAP_FACE",FACE,{"disambiguationData":[OSD([subQ1,sQuery(id+"F0.wireOp",EDGE,"E0.top"),sQuery(id+"F0.wireOp",EDGE,"E0.left"),subQ0,sQuery(id+"F0.wireOp",EDGE,"E1"),sQuery(id+"F0.wireOp",EDGE,"E2"),sQuery(id+"F0.wireOp",EDGE,"E3"),sQuery(id+"F0.wireOp",EDGE,"E4")])],"isStart":true})],"blendedInto":[makeQuery(id+"F1.opExtrude","CAP_FACE",FACE,{"disambiguationData":[OSD([subQ1,sQuery(id+"F0.wireOp",EDGE,"E0.top"),sQuery(id+"F0.wireOp",EDGE,"E0.left"),subQ0,sQuery(id+"F0.wireOp",EDGE,"E1"),sQuery(id+"F0.wireOp",EDGE,"E2"),sQuery(id+"F0.wireOp",EDGE,"E3"),sQuery(id+"F0.wireOp",EDGE,"E4")])],"isStart":true})]});}
            var Q1;
            {var subQ0=sQuery(id+"F3.wireOp",EDGE,"E8");var subQ1=sQuery(id+"F0.wireOp",EDGE,"E0.right");var subQ2=sQuery(id+"F0.wireOp",EDGE,"E0.bottom");Q1=makeQuery(id+"F4.boolean.opBoolean","MERGE",EDGE,{"derivedFrom":[makeQuery(id+"F2.opFillet","BLEND_EDGE",EDGE,{"blendedFrom":[makeQuery(id+"F1.opExtrude","SWEPT_EDGE",EDGE,{"disambiguationData":[OSD([subQ2,subQ1])]}),makeQuery(id+"F1.opExtrude","CAP_FACE",FACE,{"disambiguationData":[OSD([subQ2,sQuery(id+"F0.wireOp",EDGE,"E0.top"),sQuery(id+"F0.wireOp",EDGE,"E0.left"),subQ1,sQuery(id+"F0.wireOp",EDGE,"E1"),sQuery(id+"F0.wireOp",EDGE,"E2"),sQuery(id+"F0.wireOp",EDGE,"E3"),sQuery(id+"F0.wireOp",EDGE,"E4")])],"isStart":false})],"blendedInto":[makeQuery(id+"F1.opExtrude","CAP_FACE",FACE,{"disambiguationData":[OSD([subQ2,sQuery(id+"F0.wireOp",EDGE,"E0.top"),sQuery(id+"F0.wireOp",EDGE,"E0.left"),subQ1,sQuery(id+"F0.wireOp",EDGE,"E1"),sQuery(id+"F0.wireOp",EDGE,"E2"),sQuery(id+"F0.wireOp",EDGE,"E3"),sQuery(id+"F0.wireOp",EDGE,"E4")])],"isStart":false})]}),makeQuery(id+"F4.opExtrude","CAP_EDGE",EDGE,{"disambiguationData":[OSD([subQ0]),TDD([makeQuery(id+"F3.imprint","IMPRINT",EDGE,{"disambiguationData":[TD([[makeQuery(id+"F3.imprint","INTERSECT",VERTEX,{"derivedFrom":[makeQuery(id+"F1.opExtrude","CAP_EDGE",EDGE,{"disambiguationData":[OSD([subQ2])],"isStart":false}),subQ0]}),-1.0]])],"derivedFrom":subQ0})])],"isStart":true}),makeQuery(id+"F4.opExtrude","CAP_EDGE",EDGE,{"disambiguationData":[OSD([subQ0]),TDD([makeQuery(id+"F3.imprint","IMPRINT",EDGE,{"disambiguationData":[TD([[makeQuery(id+"F3.imprint","INTERSECT",VERTEX,{"derivedFrom":[makeQuery(id+"F1.opExtrude","CAP_EDGE",EDGE,{"disambiguationData":[OSD([subQ1])],"isStart":false}),subQ0]}),1.0]])],"derivedFrom":subQ0})])],"isStart":true})]});}
            var Q2;
            {var subQ0=sQuery(id+"F3.wireOp",EDGE,"E7");var subQ1=sQuery(id+"F0.wireOp",EDGE,"E0.left");var subQ2=sQuery(id+"F0.wireOp",EDGE,"E0.bottom");Q2=makeQuery(id+"F4.boolean.opBoolean","MERGE",EDGE,{"derivedFrom":[makeQuery(id+"F2.opFillet","BLEND_EDGE",EDGE,{"blendedFrom":[makeQuery(id+"F1.opExtrude","SWEPT_EDGE",EDGE,{"disambiguationData":[OSD([subQ2,subQ1])]}),makeQuery(id+"F1.opExtrude","CAP_FACE",FACE,{"disambiguationData":[OSD([subQ2,sQuery(id+"F0.wireOp",EDGE,"E0.top"),subQ1,sQuery(id+"F0.wireOp",EDGE,"E0.right"),sQuery(id+"F0.wireOp",EDGE,"E1"),sQuery(id+"F0.wireOp",EDGE,"E2"),sQuery(id+"F0.wireOp",EDGE,"E3"),sQuery(id+"F0.wireOp",EDGE,"E4")])],"isStart":false})],"blendedInto":[makeQuery(id+"F1.opExtrude","CAP_FACE",FACE,{"disambiguationData":[OSD([subQ2,sQuery(id+"F0.wireOp",EDGE,"E0.top"),subQ1,sQuery(id+"F0.wireOp",EDGE,"E0.right"),sQuery(id+"F0.wireOp",EDGE,"E1"),sQuery(id+"F0.wireOp",EDGE,"E2"),sQuery(id+"F0.wireOp",EDGE,"E3"),sQuery(id+"F0.wireOp",EDGE,"E4")])],"isStart":false})]}),makeQuery(id+"F4.opExtrude","CAP_EDGE",EDGE,{"disambiguationData":[OSD([subQ0]),TDD([makeQuery(id+"F3.imprint","IMPRINT",EDGE,{"disambiguationData":[TD([[makeQuery(id+"F3.imprint","INTERSECT",VERTEX,{"derivedFrom":[makeQuery(id+"F1.opExtrude","CAP_EDGE",EDGE,{"disambiguationData":[OSD([subQ2])],"isStart":false}),subQ0]}),1.0]])],"derivedFrom":subQ0})])],"isStart":true}),makeQuery(id+"F4.opExtrude","CAP_EDGE",EDGE,{"disambiguationData":[OSD([subQ0]),TDD([makeQuery(id+"F3.imprint","IMPRINT",EDGE,{"disambiguationData":[TD([[makeQuery(id+"F3.imprint","INTERSECT",VERTEX,{"derivedFrom":[makeQuery(id+"F1.opExtrude","CAP_EDGE",EDGE,{"disambiguationData":[OSD([subQ1])],"isStart":false}),subQ0]}),-1.0]])],"derivedFrom":subQ0})])],"isStart":true})]});}
            var Q3;
            {var subQ0=sQuery(id+"F3.wireOp",EDGE,"E9");var subQ1=sQuery(id+"F0.wireOp",EDGE,"E0.top");var subQ2=sQuery(id+"F0.wireOp",EDGE,"E0.left");Q3=makeQuery(id+"F4.boolean.opBoolean","MERGE",EDGE,{"derivedFrom":[makeQuery(id+"F2.opFillet","BLEND_EDGE",EDGE,{"blendedFrom":[makeQuery(id+"F1.opExtrude","SWEPT_EDGE",EDGE,{"disambiguationData":[OSD([subQ1,subQ2])]}),makeQuery(id+"F1.opExtrude","CAP_FACE",FACE,{"disambiguationData":[OSD([sQuery(id+"F0.wireOp",EDGE,"E0.bottom"),subQ1,subQ2,sQuery(id+"F0.wireOp",EDGE,"E0.right"),sQuery(id+"F0.wireOp",EDGE,"E1"),sQuery(id+"F0.wireOp",EDGE,"E2"),sQuery(id+"F0.wireOp",EDGE,"E3"),sQuery(id+"F0.wireOp",EDGE,"E4")])],"isStart":false})],"blendedInto":[makeQuery(id+"F1.opExtrude","CAP_FACE",FACE,{"disambiguationData":[OSD([sQuery(id+"F0.wireOp",EDGE,"E0.bottom"),subQ1,subQ2,sQuery(id+"F0.wireOp",EDGE,"E0.right"),sQuery(id+"F0.wireOp",EDGE,"E1"),sQuery(id+"F0.wireOp",EDGE,"E2"),sQuery(id+"F0.wireOp",EDGE,"E3"),sQuery(id+"F0.wireOp",EDGE,"E4")])],"isStart":false})]}),makeQuery(id+"F4.opExtrude","CAP_EDGE",EDGE,{"disambiguationData":[OSD([subQ0]),TDD([makeQuery(id+"F3.imprint","IMPRINT",EDGE,{"disambiguationData":[TD([[makeQuery(id+"F3.imprint","INTERSECT",VERTEX,{"derivedFrom":[makeQuery(id+"F1.opExtrude","CAP_EDGE",EDGE,{"disambiguationData":[OSD([subQ2])],"isStart":false}),subQ0]}),1.0]])],"derivedFrom":subQ0})])],"isStart":true}),makeQuery(id+"F4.opExtrude","CAP_EDGE",EDGE,{"disambiguationData":[OSD([subQ0]),TDD([makeQuery(id+"F3.imprint","IMPRINT",EDGE,{"disambiguationData":[TD([[makeQuery(id+"F3.imprint","INTERSECT",VERTEX,{"derivedFrom":[makeQuery(id+"F1.opExtrude","CAP_EDGE",EDGE,{"disambiguationData":[OSD([subQ1])],"isStart":false}),subQ0]}),-1.0]])],"derivedFrom":subQ0})])],"isStart":true})]});}
            var Q4;
            {var subQ0=sQuery(id+"F3.wireOp",EDGE,"E10");var subQ1=sQuery(id+"F0.wireOp",EDGE,"E0.top");var subQ2=sQuery(id+"F0.wireOp",EDGE,"E0.right");Q4=makeQuery(id+"F4.boolean.opBoolean","MERGE",EDGE,{"derivedFrom":[makeQuery(id+"F2.opFillet","BLEND_EDGE",EDGE,{"blendedFrom":[makeQuery(id+"F1.opExtrude","SWEPT_EDGE",EDGE,{"disambiguationData":[OSD([subQ1,subQ2])]}),makeQuery(id+"F1.opExtrude","CAP_FACE",FACE,{"disambiguationData":[OSD([sQuery(id+"F0.wireOp",EDGE,"E0.bottom"),subQ1,sQuery(id+"F0.wireOp",EDGE,"E0.left"),subQ2,sQuery(id+"F0.wireOp",EDGE,"E1"),sQuery(id+"F0.wireOp",EDGE,"E2"),sQuery(id+"F0.wireOp",EDGE,"E3"),sQuery(id+"F0.wireOp",EDGE,"E4")])],"isStart":false})],"blendedInto":[makeQuery(id+"F1.opExtrude","CAP_FACE",FACE,{"disambiguationData":[OSD([sQuery(id+"F0.wireOp",EDGE,"E0.bottom"),subQ1,sQuery(id+"F0.wireOp",EDGE,"E0.left"),subQ2,sQuery(id+"F0.wireOp",EDGE,"E1"),sQuery(id+"F0.wireOp",EDGE,"E2"),sQuery(id+"F0.wireOp",EDGE,"E3"),sQuery(id+"F0.wireOp",EDGE,"E4")])],"isStart":false})]}),makeQuery(id+"F4.opExtrude","CAP_EDGE",EDGE,{"disambiguationData":[OSD([subQ0]),TDD([makeQuery(id+"F3.imprint","IMPRINT",EDGE,{"disambiguationData":[TD([[makeQuery(id+"F3.imprint","INTERSECT",VERTEX,{"derivedFrom":[makeQuery(id+"F1.opExtrude","CAP_EDGE",EDGE,{"disambiguationData":[OSD([subQ2])],"isStart":false}),subQ0]}),-1.0]])],"derivedFrom":subQ0})])],"isStart":true}),makeQuery(id+"F4.opExtrude","CAP_EDGE",EDGE,{"disambiguationData":[OSD([subQ0]),TDD([makeQuery(id+"F3.imprint","IMPRINT",EDGE,{"disambiguationData":[TD([[makeQuery(id+"F3.imprint","INTERSECT",VERTEX,{"derivedFrom":[makeQuery(id+"F1.opExtrude","CAP_EDGE",EDGE,{"disambiguationData":[OSD([subQ1])],"isStart":false}),subQ0]}),1.0]])],"derivedFrom":subQ0})])],"isStart":true})]});}
            var Q5;
            Q5=makeQuery(id+"F4.boolean.opBoolean","COPY",EDGE,{"derivedFrom":makeQuery(id+"F4.opExtrude","CAP_EDGE",EDGE,{"disambiguationData":[OSD([sQuery(id+"F3.wireOp",EDGE,"E5")])],"isStart":true})});
            var Q6;
            Q6=makeQuery(id+"F1.opExtrude","CAP_EDGE",EDGE,{"disambiguationData":[OSD([sQuery(id+"F0.wireOp",EDGE,"E1")])],"isStart":true});
            var Q7;
            Q7=makeQuery(id+"F1.opExtrude","CAP_EDGE",EDGE,{"disambiguationData":[OSD([sQuery(id+"F0.wireOp",EDGE,"E2")])],"isStart":true});
            var Q8;
            Q8=makeQuery(id+"F1.opExtrude","CAP_EDGE",EDGE,{"disambiguationData":[OSD([sQuery(id+"F0.wireOp",EDGE,"E3")])],"isStart":true});
            var Q9;
            Q9=makeQuery(id+"F1.opExtrude","CAP_EDGE",EDGE,{"disambiguationData":[OSD([sQuery(id+"F0.wireOp",EDGE,"E4")])],"isStart":true});
            var Q10;
            Q10=makeQuery(id+"F1.opExtrude","CAP_EDGE",EDGE,{"disambiguationData":[OSD([sQuery(id+"F0.wireOp",EDGE,"E4")])],"isStart":false});
            var Q11;
            Q11=makeQuery(id+"F1.opExtrude","CAP_EDGE",EDGE,{"disambiguationData":[OSD([sQuery(id+"F0.wireOp",EDGE,"E3")])],"isStart":false});
            var Q12;
            Q12=makeQuery(id+"F1.opExtrude","CAP_EDGE",EDGE,{"disambiguationData":[OSD([sQuery(id+"F0.wireOp",EDGE,"E1")])],"isStart":false});
            var Q13;
            Q13=makeQuery(id+"F1.opExtrude","CAP_EDGE",EDGE,{"disambiguationData":[OSD([sQuery(id+"F0.wireOp",EDGE,"E2")])],"isStart":false});
            fillet(context, id + "F10", {"entities" : qUnion([Q0, Q1, Q2, Q3, Q4, Q5, Q6, Q7, Q8, Q9, Q10, Q11, Q12, Q13]), "radius" : 0.3 * mm, "tangentPropagation" : true, "allowEdgeOverflow" : false});
        }
        {
            var Q0;
            Q0=makeQuery(id+"F6.boolean.opBoolean","COPY",EDGE,{"derivedFrom":makeQuery(id+"F6.opExtrude","SWEPT_EDGE",EDGE,{"disambiguationData":[OSD([sQuery(id+"F3.wireOp",EDGE,"E5"),sQuery(id+"F5.wireOp",EDGE,"E18")])]})});
            var Q1;
            Q1=makeQuery(id+"F6.boolean.opBoolean","COPY",EDGE,{"derivedFrom":makeQuery(id+"F6.opExtrude","SWEPT_EDGE",EDGE,{"disambiguationData":[OSD([sQuery(id+"F3.wireOp",EDGE,"E5"),sQuery(id+"F5.wireOp",EDGE,"E19")])]})});
            var Q2;
            Q2=makeQuery(id+"F6.boolean.opBoolean","COPY",EDGE,{"derivedFrom":makeQuery(id+"F6.opExtrude","SWEPT_EDGE",EDGE,{"disambiguationData":[OSD([sQuery(id+"F5.wireOp",EDGE,"E17"),sQuery(id+"F5.wireOp",EDGE,"E18")])]})});
            var Q3;
            Q3=makeQuery(id+"F6.boolean.opBoolean","COPY",EDGE,{"derivedFrom":makeQuery(id+"F6.opExtrude","SWEPT_EDGE",EDGE,{"disambiguationData":[OSD([sQuery(id+"F5.wireOp",EDGE,"E17"),sQuery(id+"F5.wireOp",EDGE,"E19")])]})});
            var Q4;
            Q4=makeQuery(id+"F6.boolean.opBoolean","COPY",EDGE,{"derivedFrom":makeQuery(id+"F6.opExtrude","SWEPT_EDGE",EDGE,{"disambiguationData":[OSD([sQuery(id+"F5.wireOp",EDGE,"E17"),sQuery(id+"F5.wireOp",EDGE,"E20.2.1")])]})});
            var Q5;
            Q5=makeQuery(id+"F6.boolean.opBoolean","COPY",EDGE,{"derivedFrom":makeQuery(id+"F6.opExtrude","SWEPT_EDGE",EDGE,{"disambiguationData":[OSD([sQuery(id+"F5.wireOp",EDGE,"E17"),sQuery(id+"F5.wireOp",EDGE,"E20.2.0")])]})});
            var Q6;
            Q6=makeQuery(id+"F6.boolean.opBoolean","COPY",EDGE,{"derivedFrom":makeQuery(id+"F6.opExtrude","SWEPT_EDGE",EDGE,{"disambiguationData":[OSD([sQuery(id+"F5.wireOp",EDGE,"E17"),sQuery(id+"F5.wireOp",EDGE,"E20.1.1")])]})});
            var Q7;
            Q7=makeQuery(id+"F6.boolean.opBoolean","COPY",EDGE,{"derivedFrom":makeQuery(id+"F6.opExtrude","SWEPT_EDGE",EDGE,{"disambiguationData":[OSD([sQuery(id+"F5.wireOp",EDGE,"E17"),sQuery(id+"F5.wireOp",EDGE,"E20.1.0")])]})});
            var Q8;
            Q8=makeQuery(id+"F6.boolean.opBoolean","COPY",EDGE,{"derivedFrom":makeQuery(id+"F6.opExtrude","SWEPT_EDGE",EDGE,{"disambiguationData":[OSD([sQuery(id+"F3.wireOp",EDGE,"E5"),sQuery(id+"F5.wireOp",EDGE,"E20.1.0")])]})});
            var Q9;
            Q9=makeQuery(id+"F6.boolean.opBoolean","COPY",EDGE,{"derivedFrom":makeQuery(id+"F6.opExtrude","SWEPT_EDGE",EDGE,{"disambiguationData":[OSD([sQuery(id+"F3.wireOp",EDGE,"E5"),sQuery(id+"F5.wireOp",EDGE,"E20.1.1")])]})});
            var Q10;
            Q10=makeQuery(id+"F6.boolean.opBoolean","COPY",EDGE,{"derivedFrom":makeQuery(id+"F6.opExtrude","SWEPT_EDGE",EDGE,{"disambiguationData":[OSD([sQuery(id+"F3.wireOp",EDGE,"E5"),sQuery(id+"F5.wireOp",EDGE,"E20.2.0")])]})});
            var Q11;
            Q11=makeQuery(id+"F6.boolean.opBoolean","COPY",EDGE,{"derivedFrom":makeQuery(id+"F6.opExtrude","SWEPT_EDGE",EDGE,{"disambiguationData":[OSD([sQuery(id+"F3.wireOp",EDGE,"E5"),sQuery(id+"F5.wireOp",EDGE,"E20.2.1")])]})});
            fillet(context, id + "F11", {"entities" : qUnion([Q0, Q1, Q2, Q3, Q4, Q5, Q6, Q7, Q8, Q9, Q10, Q11]), "radius" : 1 * mm, "tangentPropagation" : true, "allowEdgeOverflow" : false});
        }
    });
